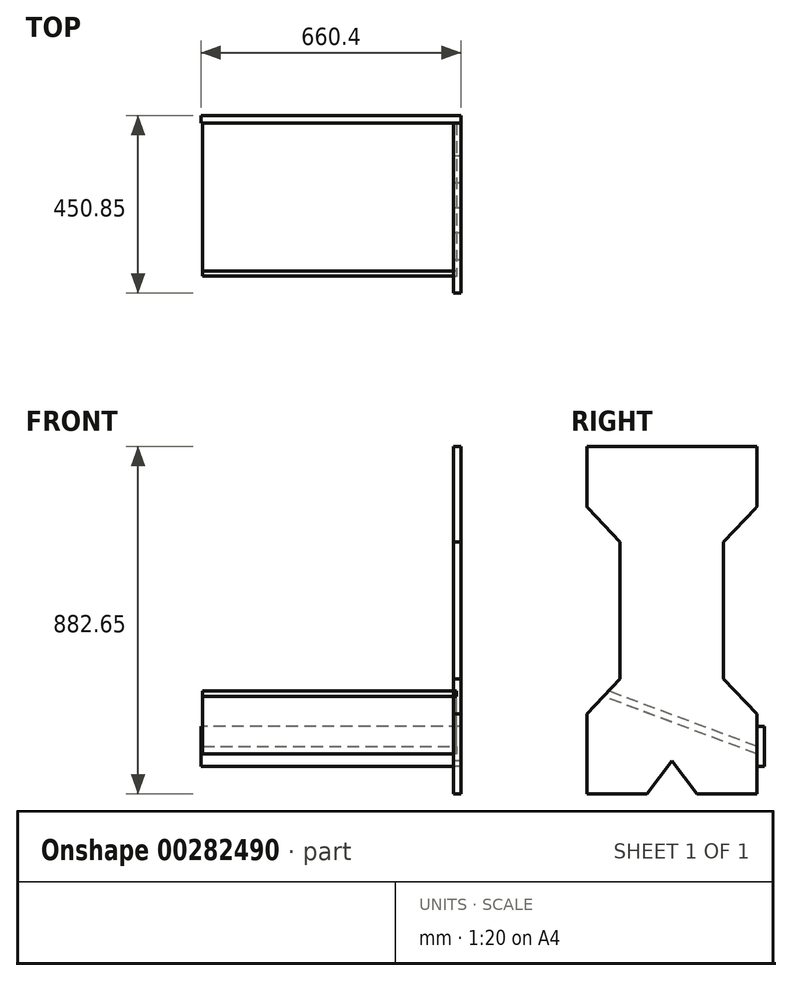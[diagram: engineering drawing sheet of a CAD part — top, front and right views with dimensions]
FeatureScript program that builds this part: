
annotation { "Feature Type Name" : "Feature", "Feature Type Description" : "" }
export const myFeature = defineFeature(function(context is Context, id is Id, definition is map)
    precondition{}
    {
        {
            var Q0;
            Q0=qCreatedBy(makeId("Right.planeOp"),FACE);
            var sketch = newSketch(context, id + "F0", { "sketchPlane" : qUnion([Q0])});
            skLineSegment(sketch, "E0.bottom", {"start": v(215.9, 76.83) * mm, "end": v(-215.9, 76.83) * mm});
            skLineSegment(sketch, "E0.top", {"start": v(215.9, -76.83) * mm, "end": v(-215.9, -76.83) * mm, "construction": true});
            skLineSegment(sketch, "E0.left", {"start": v(215.9, 76.83) * mm, "end": v(215.9, -72.8) * mm});
            skLineSegment(sketch, "E0.right", {"start": v(-215.9, 76.83) * mm, "end": v(-215.9, -73.26) * mm});
            skPoint(sketch, "E0.middle", {"position": v(0, 0) * mm});
            skLineSegment(sketch, "E1", {"start": v(-213.44, -79.43) * mm, "end": v(-131.55, -165.74) * mm});
            skLineSegment(sketch, "E2", {"start": v(213.12, -79.76) * mm, "end": v(131.55, -165.74) * mm});
            skLineSegment(sketch, "E3", {"start": v(-131.55, -165.74) * mm, "end": v(-131.55, -513.71) * mm});
            skPoint(sketch, "E4.visualSharp", {"position": v(-215.9, -76.83) * mm});
            skArc(sketch, "E4.filletArc", {"start": v(-215.9, -73.26) * mm, "mid": v(-215.26, -76.58) * mm, "end": v(-213.44, -79.43) * mm});
            skPoint(sketch, "E5.visualSharp", {"position": v(215.9, -76.83) * mm});
            skArc(sketch, "E5.filletArc", {"start": v(213.12, -79.76) * mm, "mid": v(215.18, -76.55) * mm, "end": v(215.9, -72.8) * mm});
            skLineSegment(sketch, "E6", {"start": v(-131.55, -513.71) * mm, "end": v(-215.9, -602.62) * mm});
            skLineSegment(sketch, "E7", {"start": v(-215.9, -602.62) * mm, "end": v(-215.9, -805.82) * mm});
            skLineSegment(sketch, "E8.MirrorCS", {"start": v(131.55, -165.74) * mm, "end": v(131.55, -513.71) * mm});
            skLineSegment(sketch, "E9.MirrorCS", {"start": v(131.55, -513.72) * mm, "end": v(215.9, -602.62) * mm});
            skLineSegment(sketch, "E10.MirrorCS", {"start": v(215.9, -602.62) * mm, "end": v(215.9, -805.82) * mm});
            skLineSegment(sketch, "E11", {"start": v(-131.55, -165.74) * mm, "end": v(-34.7, -165.74) * mm, "construction": true});
            skLineSegment(sketch, "E12", {"start": v(-215.9, -602.62) * mm, "end": v(-131.55, -602.62) * mm, "construction": true});
            skLineSegment(sketch, "E13", {"start": v(-215.9, -805.82) * mm, "end": v(-63.5, -805.82) * mm});
            skLineSegment(sketch, "E14", {"start": v(-63.5, -805.82) * mm, "end": v(0, -721.49) * mm});
            skLineSegment(sketch, "E15", {"start": v(0, -721.49) * mm, "end": v(63.5, -805.82) * mm});
            skLineSegment(sketch, "E16", {"start": v(63.5, -805.82) * mm, "end": v(215.9, -805.82) * mm});
            skSolve(sketch);
        }
        {
            var Q0;
            Q0 = qSketchRegion(id + "F0", true);
            extrude(context, id + "F1", {"entities" : qUnion([Q0]), "depth" : 19.05 * mm});
        }
        {
            var Q0;
            Q0=makeQuery(id+"F1.opExtrude","CAP_FACE",FACE,{"disambiguationData":[OSD([sQuery(id+"F0.wireOp",EDGE,"E0.bottom"),sQuery(id+"F0.wireOp",EDGE,"E0.left"),sQuery(id+"F0.wireOp",EDGE,"E0.right"),sQuery(id+"F0.wireOp",EDGE,"E1"),sQuery(id+"F0.wireOp",EDGE,"E2"),sQuery(id+"F0.wireOp",EDGE,"E3"),sQuery(id+"F0.wireOp",EDGE,"E4.filletArc"),sQuery(id+"F0.wireOp",EDGE,"E5.filletArc"),sQuery(id+"F0.wireOp",EDGE,"E6"),sQuery(id+"F0.wireOp",EDGE,"E7"),sQuery(id+"F0.wireOp",EDGE,"E8.MirrorCS"),sQuery(id+"F0.wireOp",EDGE,"E9.MirrorCS"),sQuery(id+"F0.wireOp",EDGE,"E10.MirrorCS"),sQuery(id+"F0.wireOp",EDGE,"E13"),sQuery(id+"F0.wireOp",EDGE,"E14"),sQuery(id+"F0.wireOp",EDGE,"E15"),sQuery(id+"F0.wireOp",EDGE,"E16")])],"isStart":true});
            var sketch = newSketch(context, id + "F2", { "sketchPlane" : qUnion([Q0])});
            skLineSegment(sketch, "E17", {"start": v(-215.9, -704.22) * mm, "end": v(173.72, -558.16) * mm});
            skLineSegment(sketch, "E18", {"start": v(-215.9, -685.17) * mm, "end": v(160.61, -544.35) * mm});
            skLineSegment(sketch, "E19", {"start": v(160.61, -544.35) * mm, "end": v(173.72, -558.16) * mm});
            skSolve(sketch);
        }
        {
            var Q0;
            {var subQ0=sQuery(id+"F2.wireOp",EDGE,"E17");Q0=makeQuery(id+"F2.imprint","IMPRINT",FACE,{"disambiguationData":[TD([[makeQuery(id+"F2.imprint","IMPRINT",EDGE,{"derivedFrom":subQ0}),1.0]])]});}
            extrude(context, id + "F3", {"entities" : qUnion([Q0]), "operationType" : NewBodyOperationType.REMOVE, "oppositeDirection" : true, "depth" : 7.62 * mm});
        }
        {
            var Q0;
            Q0=makeQuery(id+"F1.opExtrude","SWEPT_FACE",FACE,{"disambiguationData":[OSD([sQuery(id+"F0.wireOp",EDGE,"E10.MirrorCS")])]});
            var sketch = newSketch(context, id + "F4", { "sketchPlane" : qUnion([Q0])});
            skLineSegment(sketch, "E20.bottom", {"start": v(-19.05, -634.37) * mm, "end": v(641.35, -634.37) * mm});
            skLineSegment(sketch, "E20.top", {"start": v(-19.05, -735.97) * mm, "end": v(641.35, -735.97) * mm});
            skLineSegment(sketch, "E20.left", {"start": v(-19.05, -634.37) * mm, "end": v(-19.05, -735.97) * mm});
            skLineSegment(sketch, "E20.right", {"start": v(641.35, -634.37) * mm, "end": v(641.35, -735.97) * mm});
            skLineSegment(sketch, "E21", {"start": v(0, -634.37) * mm, "end": v(0, -685.17) * mm, "construction": true});
            skPoint(sketch, "E21.startSnap0", {"position": v(0, -643.9) * mm});
            skLineSegment(sketch, "E22", {"start": v(311.15, -634.37) * mm, "end": v(311.15, -735.97) * mm, "construction": true});
            skSolve(sketch);
        }
        {
            var Q0;
            Q0 = qSketchRegion(id + "F4", true);
            extrude(context, id + "F5", {"entities" : qUnion([Q0]), "depth" : 19.05 * mm});
        }
        {
            var Q0;
            {var subQ0=sQuery(id+"F0.wireOp",EDGE,"E8.MirrorCS");var subQ1=sQuery(id+"F0.wireOp",EDGE,"E6");var subQ2=sQuery(id+"F0.wireOp",EDGE,"E5.filletArc");var subQ3=sQuery(id+"F0.wireOp",EDGE,"E4.filletArc");var subQ4=sQuery(id+"F0.wireOp",EDGE,"E3");var subQ5=sQuery(id+"F0.wireOp",EDGE,"E2");var subQ6=sQuery(id+"F0.wireOp",EDGE,"E0.bottom");var subQ7=sQuery(id+"F0.wireOp",EDGE,"E1");var subQ8=sQuery(id+"F0.wireOp",EDGE,"E0.left");var subQ9=sQuery(id+"F0.wireOp",EDGE,"E0.right");var subQ10=sQuery(id+"F0.wireOp",EDGE,"E9.MirrorCS");var subQ11=sQuery(id+"F0.wireOp",EDGE,"E10.MirrorCS");Q0=makeQuery(id+"F3.boolean.opBoolean","SPLIT",FACE,{"disambiguationData":[TD([makeQuery(id+"F1.opExtrude","SWEPT_FACE",FACE,{"disambiguationData":[OSD([subQ6])]})])],"derivedFrom":makeQuery(id+"F1.opExtrude","CAP_FACE",FACE,{"disambiguationData":[OSD([subQ6,subQ8,subQ9,subQ7,subQ5,subQ4,subQ3,subQ2,subQ1,sQuery(id+"F0.wireOp",EDGE,"E7"),subQ0,subQ10,subQ11,sQuery(id+"F0.wireOp",EDGE,"E13"),sQuery(id+"F0.wireOp",EDGE,"E14"),sQuery(id+"F0.wireOp",EDGE,"E15"),sQuery(id+"F0.wireOp",EDGE,"E16")])],"isStart":true})});}
            var sketch = newSketch(context, id + "F6", { "sketchPlane" : qUnion([Q0])});
            skLineSegment(sketch, "E23", {"start": v(-215.9, -685.17) * mm, "end": v(-215.9, -704.22) * mm});
            skLineSegment(sketch, "E24", {"start": v(-215.9, -704.22) * mm, "end": v(173.36, -558.5) * mm});
            skLineSegment(sketch, "E25", {"start": v(173.36, -558.5) * mm, "end": v(160.61, -544.35) * mm});
            skLineSegment(sketch, "E26", {"start": v(160.61, -544.35) * mm, "end": v(-215.9, -685.17) * mm});
            skSolve(sketch);
        }
        {
            var Q0;
            Q0=makeQuery(id+"F6.imprint","IMPRINT",FACE,{"disambiguationData":[TD([[makeQuery(id+"F6.imprint","IMPRINT",EDGE,{"derivedFrom":sQuery(id+"F6.wireOp",EDGE,"E23")}),1.0]])]});
            extrude(context, id + "F7", {"entities" : qUnion([Q0]), "depth" : 637.54 * mm});
        }
    });
